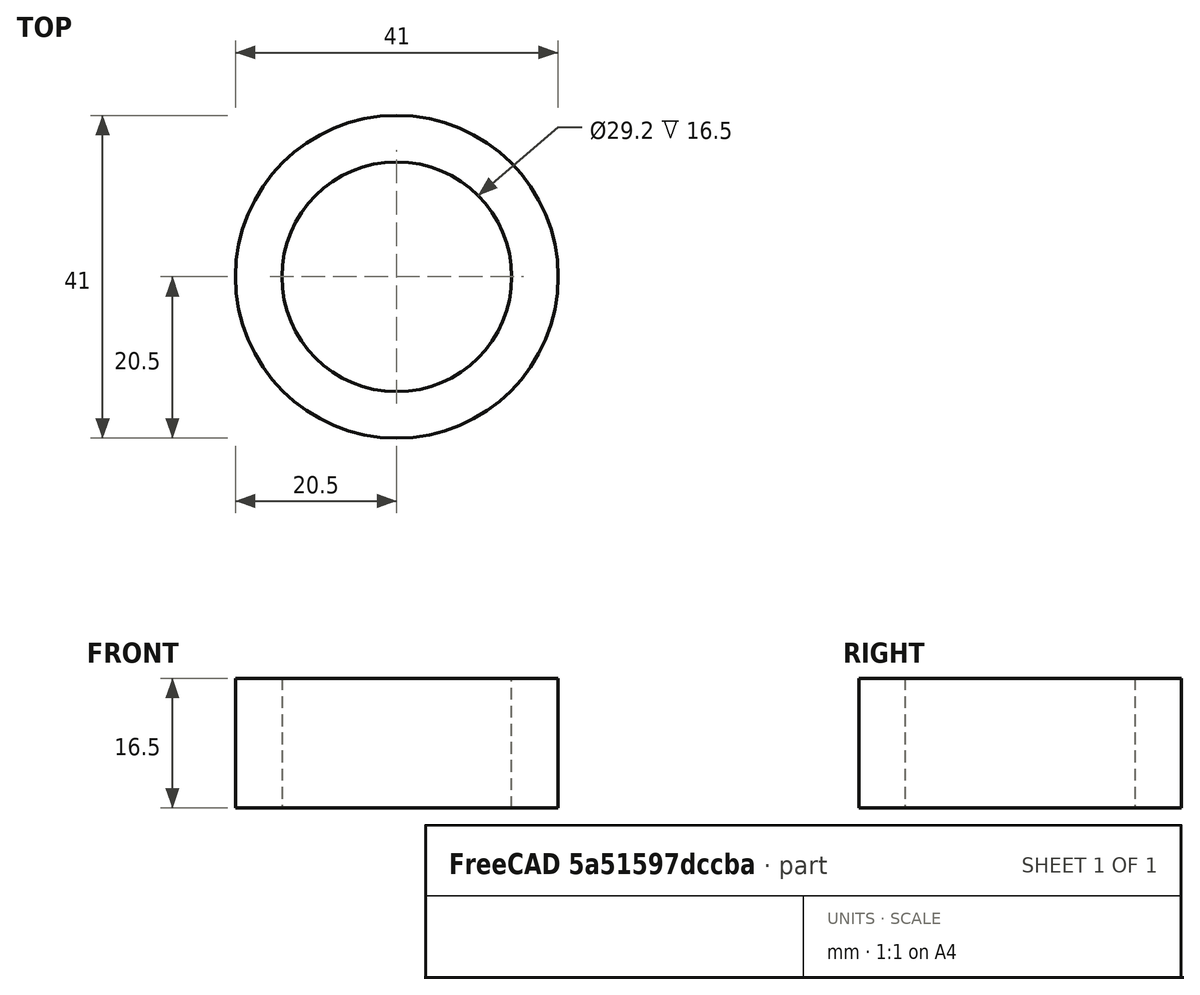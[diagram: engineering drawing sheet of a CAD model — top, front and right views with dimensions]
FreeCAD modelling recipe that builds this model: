
FCSTD DOCUMENT  (FreeCAD 0.19R24291 (Git))
Label: TurbidityAdapter1
License: All rights reserved
LicenseURL: http://en.wikipedia.org/wiki/All_rights_reserved
objects: Sketcher::SketchObject×1, PartDesign::Pad×1, PartDesign::Body×1
note: 4 computed .brp shape members not serialized (recipe doc carries the construction recipe); baked Part::Feature solids carry a one-line shape summary decoded from their .brp

FEATURE [Sketcher::SketchObject] Sketch
  FullyConstrained = true
  MapMode = 5
  Support = -> [XY_Plane]
  sketch-geometry (2):
    g0: Circle CenterX=0 CenterY=0 CenterZ=0 NormalX=0 NormalY=0 NormalZ=1 AngleXU=0 Radius=20.5
    g1: Circle CenterX=0 CenterY=0 CenterZ=0 NormalX=0 NormalY=0 NormalZ=1 AngleXU=0 Radius=14.6
  constraints (4):
    c: Coincident(g0,g-1)
    c: Radius(g0) = 20.5
    c: Coincident(g1,g0)
    c: Radius(g1) = 14.6
FEATURE [PartDesign::Pad] Pad
  Direction = (1,1,1)
  Length = 16.5
  Length2 = 100
  Profile = -> Sketch
  Type = 0
FEATURE [PartDesign::Body] Body
  Group = -> [Sketch,Pad]
  Origin = -> Origin
  Tip = -> Pad
